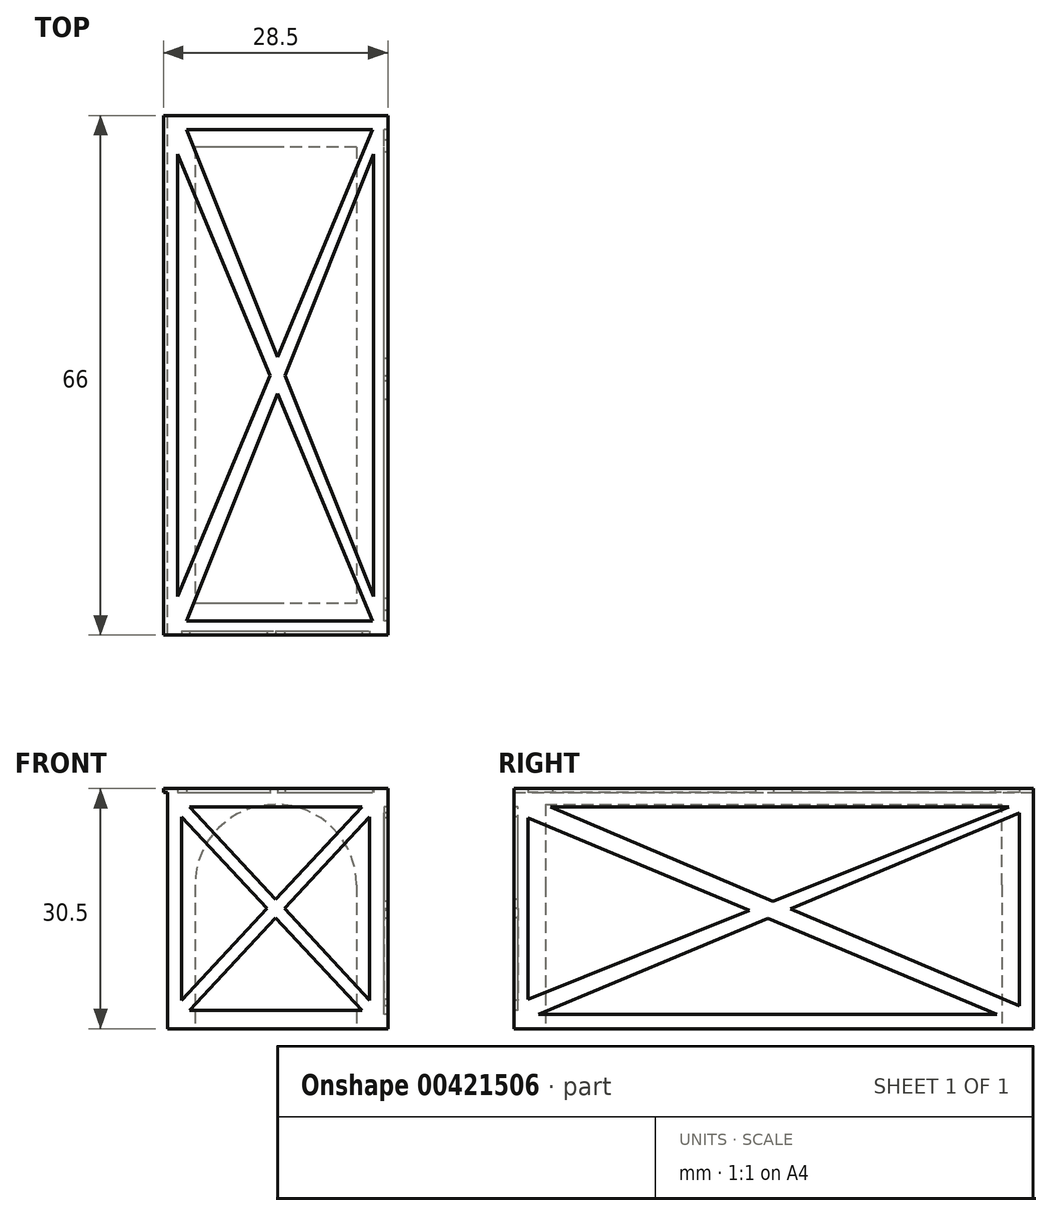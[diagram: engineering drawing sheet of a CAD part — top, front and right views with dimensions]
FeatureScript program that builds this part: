
annotation { "Feature Type Name" : "Feature", "Feature Type Description" : "" }
export const myFeature = defineFeature(function(context is Context, id is Id, definition is map)
    precondition{}
    {
        {
            var Q0;
            Q0=qCreatedBy(makeId("Top.planeOp"),FACE);
            var sketch = newSketch(context, id + "F0", { "sketchPlane" : qUnion([Q0])});
            skLineSegment(sketch, "E0.bottom", {"start": v(13.75, -33) * mm, "end": v(-13.75, -33) * mm});
            skLineSegment(sketch, "E0.top", {"start": v(13.75, 33) * mm, "end": v(-13.75, 33) * mm});
            skLineSegment(sketch, "E0.left", {"start": v(13.75, -33) * mm, "end": v(13.75, 33) * mm});
            skLineSegment(sketch, "E0.right", {"start": v(-13.75, -33) * mm, "end": v(-13.75, 33) * mm});
            skPoint(sketch, "E0.middle", {"position": v(0, 0) * mm});
            skSolve(sketch);
        }
        {
            var Q0;
            Q0 = qSketchRegion(id + "F0", true);
            extrude(context, id + "F1", {"entities" : qUnion([Q0]), "depth" : 30 * mm});
        }
        {
            var Q0;
            Q0=makeQuery(id+"F1.opExtrude","SWEPT_FACE",FACE,{"disambiguationData":[OSD([sQuery(id+"F0.wireOp",EDGE,"E0.left")])]});
            var sketch = newSketch(context, id + "F2", { "sketchPlane" : qUnion([Q0])});
            skLineSegment(sketch, "E1", {"start": v(-33, 30) * mm, "end": v(-33, 0) * mm});
            skLineSegment(sketch, "E2", {"start": v(-33, 0) * mm, "end": v(33, 0) * mm});
            skLineSegment(sketch, "E3", {"start": v(33, 0) * mm, "end": v(33, 30) * mm});
            skLineSegment(sketch, "E4", {"start": v(33, 30) * mm, "end": v(-33, 30) * mm});
            skLineSegment(sketch, "E5", {"start": v(-31.2, 26.8) * mm, "end": v(-31.2, 3.73) * mm});
            skLineSegment(sketch, "E6", {"start": v(-29.87, 1.8) * mm, "end": v(28.37, 1.8) * mm});
            skLineSegment(sketch, "E7", {"start": v(31.2, 2.92) * mm, "end": v(31.2, 27.43) * mm});
            skLineSegment(sketch, "E8", {"start": v(-28.37, 28.2) * mm, "end": v(29.87, 28.2) * mm});
            skLineSegment(sketch, "E9.0", {"start": v(-31.2, 26.8) * mm, "end": v(-3.08, 15) * mm});
            skLineSegment(sketch, "E10.0", {"start": v(-28.37, 28.2) * mm, "end": v(-0.1, 16.2) * mm});
            skLineSegment(sketch, "E11.0", {"start": v(-29.87, 1.8) * mm, "end": v(-0.75, 14.02) * mm});
            skLineSegment(sketch, "E12.0", {"start": v(-31.2, 3.73) * mm, "end": v(-3.08, 15) * mm});
            skLineSegment(sketch, "E13.trimOffspring", {"start": v(-0.1, 16.2) * mm, "end": v(29.87, 28.2) * mm});
            skLineSegment(sketch, "E14.trimOffspring", {"start": v(2.15, 15.24) * mm, "end": v(31.2, 2.92) * mm});
            skLineSegment(sketch, "E15.trimOffspring", {"start": v(2.15, 15.24) * mm, "end": v(31.2, 27.43) * mm});
            skLineSegment(sketch, "E16.trimOffspring", {"start": v(-0.75, 14.02) * mm, "end": v(28.37, 1.8) * mm});
            skSolve(sketch);
        }
        {
            var Q0;
            Q0 = qSketchRegion(id + "F2", true);
            extrude(context, id + "F3", {"entities" : qUnion([Q0]), "operationType" : NewBodyOperationType.ADD, "depth" : 0.5 * mm});
        }
        {
            var Q0;
            {var subQ0=sQuery(id+"F2.wireOp",EDGE,"E4");Q0=makeQuery(id+"Fi2ehXyChXqGkiH_1.1.F3.boolean.opBoolean","MERGE",FACE,{"derivedFrom":[makeQuery(id+"F3.boolean.opBoolean","MERGE",FACE,{"derivedFrom":[makeQuery(id+"F1.opExtrude","CAP_FACE",FACE,{"disambiguationData":[OSD([sQuery(id+"F0.wireOp",EDGE,"E0.bottom"),sQuery(id+"F0.wireOp",EDGE,"E0.top"),sQuery(id+"F0.wireOp",EDGE,"E0.left"),sQuery(id+"F0.wireOp",EDGE,"E0.right")])],"isStart":false}),makeQuery(id+"F3.opExtrude","SWEPT_FACE",FACE,{"disambiguationData":[OSD([subQ0])]})]}),makeQuery(id+"Fi2ehXyChXqGkiH_1.1.F3.opExtrude","SWEPT_FACE",FACE,{"disambiguationData":[OSD([subQ0])]})]});}
            var sketch = newSketch(context, id + "F4", { "sketchPlane" : qUnion([Q0])});
            skLineSegment(sketch, "E17", {"start": v(-14.25, -33) * mm, "end": v(-14.25, 33) * mm});
            skLineSegment(sketch, "E18", {"start": v(-14.25, 33) * mm, "end": v(14.25, 33) * mm});
            skLineSegment(sketch, "E19", {"start": v(14.25, 33) * mm, "end": v(14.25, -33) * mm});
            skLineSegment(sketch, "E20", {"start": v(14.25, -33) * mm, "end": v(-14.25, -33) * mm});
            skLineSegment(sketch, "E21.0", {"start": v(12.29, -31.2) * mm, "end": v(-11.31, -31.2) * mm});
            skLineSegment(sketch, "E22.0", {"start": v(-11.31, 31.2) * mm, "end": v(12.29, 31.2) * mm});
            skLineSegment(sketch, "E23.0", {"start": v(-12.45, -28.11) * mm, "end": v(-12.45, 28.11) * mm});
            skLineSegment(sketch, "E24.0", {"start": v(12.45, 28.11) * mm, "end": v(12.45, -28.11) * mm});
            skLineSegment(sketch, "E25.0", {"start": v(-12.45, 28.11) * mm, "end": v(-0.73, 0) * mm});
            skLineSegment(sketch, "E26.0", {"start": v(-11.31, 31.2) * mm, "end": v(0.25, 2.34) * mm});
            skLineSegment(sketch, "E27.0", {"start": v(-11.31, -31.2) * mm, "end": v(0.25, -2.34) * mm});
            skLineSegment(sketch, "E28.0", {"start": v(-12.45, -28.11) * mm, "end": v(-0.73, 0) * mm});
            skLineSegment(sketch, "E29.trimOffspring", {"start": v(0.25, 2.34) * mm, "end": v(12.29, 31.2) * mm});
            skLineSegment(sketch, "E30.trimOffspring", {"start": v(1.19, 0) * mm, "end": v(12.45, -28.11) * mm});
            skLineSegment(sketch, "E31.trimOffspring", {"start": v(1.19, 0) * mm, "end": v(12.45, 28.11) * mm});
            skLineSegment(sketch, "E32.trimOffspring", {"start": v(0.25, -2.34) * mm, "end": v(12.29, -31.2) * mm});
            skSolve(sketch);
        }
        {
            var Q0;
            Q0 = qSketchRegion(id + "F4", true);
            extrude(context, id + "F5", {"entities" : qUnion([Q0]), "operationType" : NewBodyOperationType.ADD, "depth" : 0.5 * mm});
        }
        {
            var Q0;
            {var subQ0=sQuery(id+"F2.wireOp",EDGE,"E1");Q0=makeQuery(id+"F5.boolean.opBoolean","MERGE",FACE,{"derivedFrom":[makeQuery(id+"Fi2ehXyChXqGkiH_1.1.F3.boolean.opBoolean","MERGE",FACE,{"derivedFrom":[makeQuery(id+"F3.boolean.opBoolean","MERGE",FACE,{"derivedFrom":[makeQuery(id+"F1.opExtrude","SWEPT_FACE",FACE,{"disambiguationData":[OSD([sQuery(id+"F0.wireOp",EDGE,"E0.bottom")])]}),makeQuery(id+"F3.opExtrude","SWEPT_FACE",FACE,{"disambiguationData":[OSD([subQ0])]})]}),makeQuery(id+"Fi2ehXyChXqGkiH_1.1.F3.opExtrude","SWEPT_FACE",FACE,{"disambiguationData":[OSD([subQ0])]})]}),makeQuery(id+"F5.opExtrude","SWEPT_FACE",FACE,{"disambiguationData":[OSD([sQuery(id+"F4.wireOp",EDGE,"E20")])]})]});}
            var sketch = newSketch(context, id + "F6", { "sketchPlane" : qUnion([Q0])});
            skLineSegment(sketch, "E33.0", {"start": v(-10.96, 2.3) * mm, "end": v(10.96, 2.3) * mm});
            skLineSegment(sketch, "E33.1", {"start": v(-11.95, 26.89) * mm, "end": v(-11.95, 3.61) * mm});
            skLineSegment(sketch, "E33.2", {"start": v(10.96, 28.2) * mm, "end": v(-10.96, 28.2) * mm});
            skLineSegment(sketch, "E33.3", {"start": v(11.95, 3.61) * mm, "end": v(11.95, 26.89) * mm});
            skLineSegment(sketch, "E34.0", {"start": v(-11.95, 26.89) * mm, "end": v(-1.1, 15.25) * mm});
            skLineSegment(sketch, "E35.0", {"start": v(-10.96, 28.2) * mm, "end": v(0, 16.44) * mm});
            skLineSegment(sketch, "E36.0", {"start": v(-10.96, 2.3) * mm, "end": v(0, 14.06) * mm});
            skLineSegment(sketch, "E37.0", {"start": v(-11.95, 3.61) * mm, "end": v(-1.1, 15.25) * mm});
            skLineSegment(sketch, "E38.trimOffspring", {"start": v(1.1, 15.25) * mm, "end": v(11.95, 3.61) * mm});
            skLineSegment(sketch, "E39.trimOffspring", {"start": v(0, 16.44) * mm, "end": v(10.96, 28.2) * mm});
            skLineSegment(sketch, "E40.trimOffspring", {"start": v(1.1, 15.25) * mm, "end": v(11.95, 26.89) * mm});
            skLineSegment(sketch, "E41.trimOffspring", {"start": v(0, 14.06) * mm, "end": v(10.96, 2.3) * mm});
            skSolve(sketch);
        }
        {
            var Q0;
            Q0 = qSketchRegion(id + "F6", true);
            extrude(context, id + "F7", {"entities" : qUnion([Q0]), "operationType" : NewBodyOperationType.REMOVE, "oppositeDirection" : true, "depth" : 0.5 * mm});
        }
        {
            var Q0;
            {var subQ0=sQuery(id+"F2.wireOp",EDGE,"E2");Q0=makeQuery(id+"Fi2ehXyChXqGkiH_1.1.F3.boolean.opBoolean","MERGE",FACE,{"derivedFrom":[makeQuery(id+"F3.boolean.opBoolean","MERGE",FACE,{"derivedFrom":[makeQuery(id+"F1.opExtrude","CAP_FACE",FACE,{"disambiguationData":[OSD([sQuery(id+"F0.wireOp",EDGE,"E0.bottom"),sQuery(id+"F0.wireOp",EDGE,"E0.top"),sQuery(id+"F0.wireOp",EDGE,"E0.left"),sQuery(id+"F0.wireOp",EDGE,"E0.right")])],"isStart":true}),makeQuery(id+"F3.opExtrude","SWEPT_FACE",FACE,{"disambiguationData":[OSD([subQ0])]})]}),makeQuery(id+"Fi2ehXyChXqGkiH_1.1.F3.opExtrude","SWEPT_FACE",FACE,{"disambiguationData":[OSD([subQ0])]})]});}
            var sketch = newSketch(context, id + "F8", { "sketchPlane" : qUnion([Q0])});
            skLineSegment(sketch, "E42.bottom", {"start": v(10.25, -29) * mm, "end": v(-10.25, -29) * mm});
            skLineSegment(sketch, "E42.top", {"start": v(10.25, 29) * mm, "end": v(-10.25, 29) * mm});
            skLineSegment(sketch, "E42.left", {"start": v(10.25, -29) * mm, "end": v(10.25, 29) * mm});
            skLineSegment(sketch, "E42.right", {"start": v(-10.25, -29) * mm, "end": v(-10.25, 29) * mm});
            skPoint(sketch, "E42.middle", {"position": v(0, 0) * mm});
            skSolve(sketch);
        }
        {
            var Q0;
            Q0 = qSketchRegion(id + "F8", true);
            extrude(context, id + "F9", {"entities" : qUnion([Q0]), "operationType" : NewBodyOperationType.REMOVE, "oppositeDirection" : true, "depth" : (30.5 - 2) * mm});
        }
        {
            var Q0;
            Q0=makeQuery(id+"F9.boolean.opBoolean","COPY",EDGE,{"derivedFrom":makeQuery(id+"F9.opExtrude","CAP_EDGE",EDGE,{"disambiguationData":[OSD([sQuery(id+"F8.wireOp",EDGE,"E42.right")])],"isStart":false})});
            fillet(context, id + "F10", {"entities" : qUnion([Q0]), "radius" : (20.5 / 2) * mm, "tangentPropagation" : true, "allowEdgeOverflow" : false});
        }
        {
            var Q0;
            Q0=makeQuery(id+"F9.boolean.opBoolean","COPY",EDGE,{"derivedFrom":makeQuery(id+"F9.opExtrude","CAP_EDGE",EDGE,{"disambiguationData":[OSD([sQuery(id+"F8.wireOp",EDGE,"E42.left")])],"isStart":false})});
            fillet(context, id + "F11", {"entities" : qUnion([Q0]), "radius" : (20.5 / 2) * mm, "tangentPropagation" : true, "allowEdgeOverflow" : false});
        }
    });
